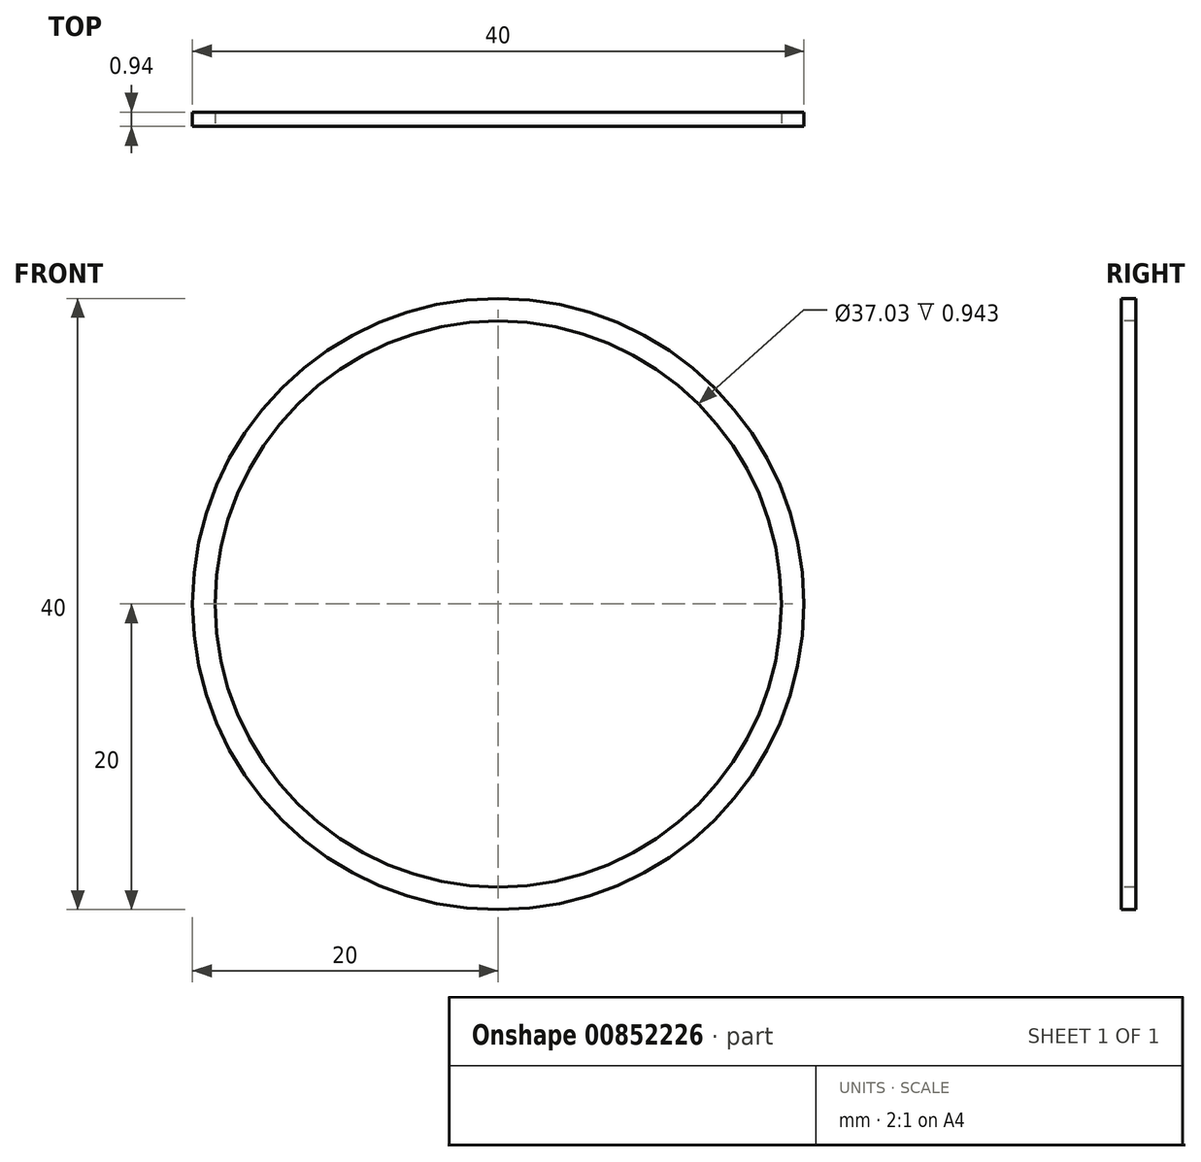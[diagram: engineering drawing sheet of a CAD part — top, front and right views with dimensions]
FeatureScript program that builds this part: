
annotation { "Feature Type Name" : "Feature", "Feature Type Description" : "" }
export const myFeature = defineFeature(function(context is Context, id is Id, definition is map)
    precondition{}
    {
        {
            var Q0;
            Q0=qCreatedBy(makeId("Top.planeOp"),FACE);
            var sketch = newSketch(context, id + "F0", { "sketchPlane" : qUnion([Q0])});
            skLineSegment(sketch, "E0", {"start": v(0, 0) * mm, "end": v(0, 75) * mm, "construction": true});
            skLineSegment(sketch, "E1", {"start": v(-20, -6.15) * mm, "end": v(-20, 78.13) * mm, "construction": true});
            skLineSegment(sketch, "E2", {"start": v(-8, -9.89) * mm, "end": v(-8, 77.24) * mm, "construction": true});
            skLineSegment(sketch, "E3", {"start": v(-8, 0) * mm, "end": v(-8, 5) * mm});
            skLineSegment(sketch, "E4", {"start": v(-8, 5) * mm, "end": v(-12.33, 7.5) * mm});
            skLineSegment(sketch, "E5", {"start": v(-12.33, 7.5) * mm, "end": v(-15.62, 11.27) * mm});
            skLineSegment(sketch, "E6", {"start": v(-15.62, 11.27) * mm, "end": v(-17.63, 15.85) * mm});
            skLineSegment(sketch, "E7", {"start": v(-17.63, 15.85) * mm, "end": v(-18.51, 20.77) * mm});
            skLineSegment(sketch, "E8.bottom", {"start": v(-18.51, 20.77) * mm, "end": v(-20, 20.77) * mm});
            skLineSegment(sketch, "E8.top", {"start": v(-18.51, 21.7) * mm, "end": v(-20, 21.7) * mm});
            skLineSegment(sketch, "E8.left", {"start": v(-18.51, 20.77) * mm, "end": v(-18.51, 21.7) * mm});
            skLineSegment(sketch, "E8.right", {"start": v(-20, 20.77) * mm, "end": v(-20, 21.7) * mm});
            skSolve(sketch);
        }
        {
            var Q0;
            Q0=sQuery(id+"F0.wireOp",EDGE,"E7");
            var Q1;
            Q1=sQuery(id+"F0.wireOp",EDGE,"E6");
            var Q2;
            Q2=sQuery(id+"F0.wireOp",EDGE,"E5");
            var Q3;
            Q3=sQuery(id+"F0.wireOp",EDGE,"E4");
            var Q4;
            Q4=sQuery(id+"F0.wireOp",EDGE,"E3");
            var Q5;
            Q5=sQuery(id+"F0.wireOp",EDGE,"E0");
            revolve(context, id + "F1", {"bodyType" : ToolBodyType.SURFACE, "surfaceOperationType" : NewSurfaceOperationType.NEW, "surfaceEntities" : qUnion([Q0, Q1, Q2, Q3, Q4]), "axis" : qUnion([Q5]), "revolveType" : RevolveType.FULL});
        }
        {
            var Q0;
            Q0=makeQuery(id+"F0.imprint","IMPRINT",FACE,{"disambiguationData":[TD([[makeQuery(id+"F0.imprint","IMPRINT",EDGE,{"derivedFrom":sQuery(id+"F0.wireOp",EDGE,"E8.bottom")}),-1.0]])]});
            var Q1;
            Q1=sQuery(id+"F0.wireOp",EDGE,"E0");
            revolve(context, id + "F2", {"surfaceOperationType" : NewSurfaceOperationType.NEW, "entities" : qUnion([Q0]), "axis" : qUnion([Q1]), "revolveType" : RevolveType.FULL});
        }
    });
